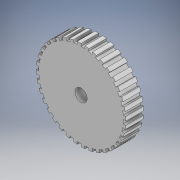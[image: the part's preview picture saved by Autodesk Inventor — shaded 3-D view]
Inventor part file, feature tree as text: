
AUTODESK INVENTOR PART (.ipt)
format: ipt  version: 2022 (Build 260153000, 153)  size: 326,144 bytes
history: native  units: in
note: dims shown in document units (in); Inventor stores cm internally (conversion verified against a paired STEP export)
features: sketch x6, extrude x3, plane x1
ambient origin geometry x8: Origin, YZ Plane, XZ Plane, XY Plane, X Axis, Y Axis, Z Axis, Center Point
bodies: Solid1 (feature_tree)
feature tree (10):
  extrude  "Extrusion1"  Depth=14.1732in TaperAngle=360.0deg
  extrude  "Extrusion2"  Depth=0.3386in
  sketch  "Sketch3"  dims[d12=0.3893in d13=0.0in d14=0.2756in]
  sketch  "Sketch4"  dims[d17=0.4134in]
  plane  "Work Plane1"
  extrude  "Extrusion5"  Depth=0.2756in
  sketch  "Sketch6"  dims[d22=0.0024in]
  sketch  "Sketch7"  dims[d23=0.2283in d24=0.3661in d25=0.0in d30=0.2598in d26=0.0197in d27=0.0344in d28=0.0197in d29=0.0344in]
  sketch  "Sketch1"  dims[d3=0.0687in d5=14.1732in d7=360.0deg]
  sketch  "Sketch2"  dims[d9=0.3386in d10=0.0in d11=0.2283in]
